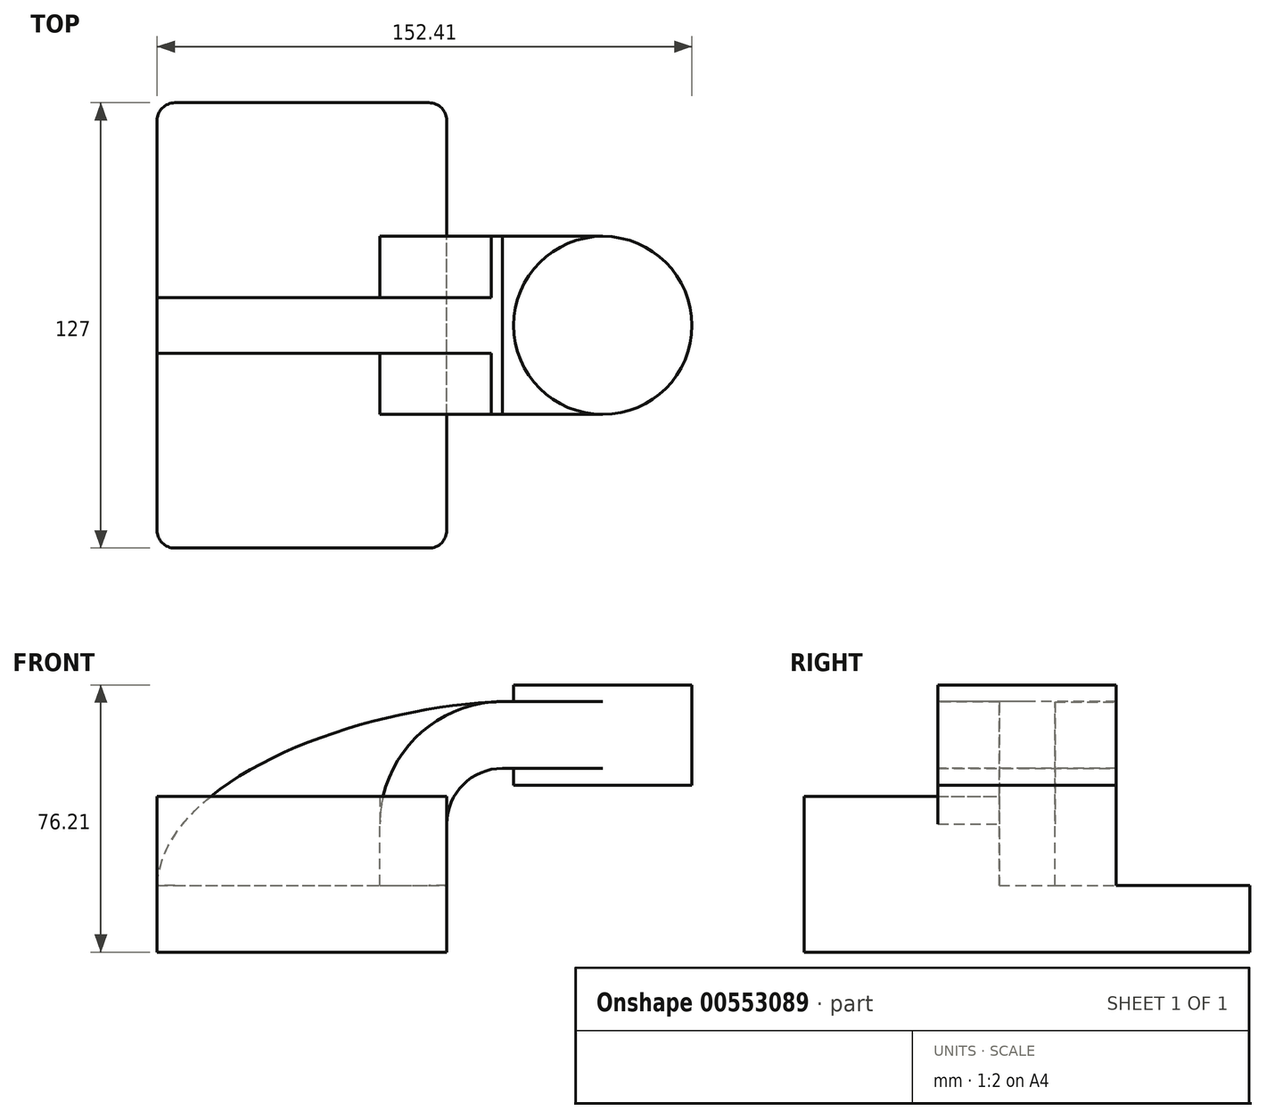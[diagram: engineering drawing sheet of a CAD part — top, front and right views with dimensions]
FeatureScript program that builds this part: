
annotation { "Feature Type Name" : "Feature", "Feature Type Description" : "" }
export const myFeature = defineFeature(function(context is Context, id is Id, definition is map)
    precondition{}
    {
        {
            var Q0;
            Q0=qCreatedBy(makeId("Front.planeOp"),FACE);
            var sketch = newSketch(context, id + "F0", { "sketchPlane" : qUnion([Q0])});
            skLineSegment(sketch, "E0.rect.bottom", {"start": v(-41.28, 9.52) * mm, "end": v(41.28, 9.52) * mm});
            skLineSegment(sketch, "E0.rect.top", {"start": v(-41.28, -9.52) * mm, "end": v(41.28, -9.52) * mm});
            skLineSegment(sketch, "E0.rect.left", {"start": v(-41.28, 9.52) * mm, "end": v(-41.28, -9.52) * mm});
            skLineSegment(sketch, "E0.rect.right", {"start": v(41.28, 9.52) * mm, "end": v(41.28, -9.52) * mm});
            skPoint(sketch, "E0.rect.middle", {"position": v(0, 0) * mm});
            skLineSegment(sketch, "E1", {"start": v(41.28, 9.52) * mm, "end": v(41.28, 27) * mm});
            skArc(sketch, "E2", {"start": v(41.28, 27) * mm, "mid": v(45.92, 38.23) * mm, "end": v(57.15, 42.88) * mm});
            skLineSegment(sketch, "E3", {"start": v(57.15, 42.88) * mm, "end": v(85.72, 42.88) * mm});
            skLineSegment(sketch, "E4.rect.bottom", {"start": v(60.32, 38.1) * mm, "end": v(111.12, 38.1) * mm});
            skLineSegment(sketch, "E4.rect.top", {"start": v(60.32, 66.68) * mm, "end": v(111.12, 66.68) * mm});
            skLineSegment(sketch, "E4.rect.left", {"start": v(60.32, 38.1) * mm, "end": v(60.32, 66.68) * mm});
            skLineSegment(sketch, "E4.rect.right", {"start": v(111.13, 38.1) * mm, "end": v(111.12, 66.68) * mm});
            skPoint(sketch, "E4.rect.middle", {"position": v(85.72, 52.39) * mm});
            skLineSegment(sketch, "E5.0", {"start": v(57.15, 61.93) * mm, "end": v(85.72, 61.93) * mm});
            skArc(sketch, "E5.1", {"start": v(22.23, 27) * mm, "mid": v(32.45, 51.7) * mm, "end": v(57.15, 61.93) * mm});
            skLineSegment(sketch, "E5.2", {"start": v(22.23, 9.52) * mm, "end": v(22.23, 27) * mm});
            skLineSegment(sketch, "E6", {"start": v(85.72, 38.1) * mm, "end": v(85.72, 66.68) * mm});
            skFitSpline(sketch, "E7", {"points": [v(-41.28, 9.53) * mm, v(57.15, 61.93) * mm], "startDerivative": vector(5.2, 92.34) * mm, "endDerivative": vector(120.92, 4.22) * mm});
            skSolve(sketch);
        }
        {
            var Q0;
            Q0=makeQuery(id+"F0.imprint","IMPRINT",FACE,{"disambiguationData":[TD([[makeQuery(id+"F0.imprint","IMPRINT",EDGE,{"derivedFrom":sQuery(id+"F0.wireOp",EDGE,"E0.rect.top")}),1.0]])]});
            extrude(context, id + "F1", {"entities" : qUnion([Q0]), "endBound" : BoundingType.SYMMETRIC, "depth" : 127 * mm});
        }
        {
            var Q0;
            {var subQ9=sQuery(id+"F0.wireOp",EDGE,"E1");Q0=makeQuery(id+"F0.imprint","IMPRINT",FACE,{"disambiguationData":[TD([[makeQuery(id+"F0.imprint","IMPRINT",EDGE,{"derivedFrom":subQ9}),1.0]])]});}
            var Q1;
            {var subQ0=sQuery(id+"F0.wireOp",EDGE,"E6");var subQ1=sQuery(id+"F0.wireOp",EDGE,"E3");var subQ2=makeQuery(id+"F0.imprint","INTERSECT",VERTEX,{"derivedFrom":[subQ1,subQ0]});Q1=makeQuery(id+"F0.imprint","IMPRINT",FACE,{"disambiguationData":[TD([[makeQuery(id+"F0.imprint","IMPRINT",EDGE,{"disambiguationData":[TD([[subQ2,1.0]])],"derivedFrom":subQ1}),1.0]])]});}
            extrude(context, id + "F2", {"entities" : qUnion([Q0, Q1]), "operationType" : NewBodyOperationType.ADD, "endBound" : BoundingType.SYMMETRIC, "depth" : 50.8 * mm});
        }
        {
            var Q0;
            {var subQ3=sQuery(id+"F0.wireOp",EDGE,"E5.2");Q0=makeQuery(id+"F0.imprint","IMPRINT",FACE,{"disambiguationData":[TD([[makeQuery(id+"F0.imprint","IMPRINT",EDGE,{"derivedFrom":subQ3}),1.0]])]});}
            extrude(context, id + "F3", {"entities" : qUnion([Q0]), "operationType" : NewBodyOperationType.ADD, "endBound" : BoundingType.SYMMETRIC, "depth" : 15.88 * mm});
        }
        {
            var Q0;
            {var subQ5=sQuery(id+"F0.wireOp",EDGE,"E4.rect.right");Q0=makeQuery(id+"F0.imprint","IMPRINT",FACE,{"disambiguationData":[TD([[makeQuery(id+"F0.imprint","IMPRINT",EDGE,{"derivedFrom":subQ5}),1.0]])]});}
            var Q1;
            Q1=sQuery(id+"F0.wireOp",EDGE,"E6");
            revolve(context, id + "F4", {"operationType" : NewBodyOperationType.ADD, "entities" : qUnion([Q0]), "axis" : qUnion([Q1]), "revolveType" : RevolveType.FULL});
        }
        {
            var Q0;
            Q0=makeQuery(id+"F1.opExtrude","CAP_EDGE",EDGE,{"disambiguationData":[OSD([sQuery(id+"F0.wireOp",EDGE,"E0.rect.right")])],"isStart":false});
            var Q1;
            Q1=makeQuery(id+"F1.opExtrude","CAP_EDGE",EDGE,{"disambiguationData":[OSD([sQuery(id+"F0.wireOp",EDGE,"E0.rect.left")])],"isStart":false});
            var Q2;
            Q2=makeQuery(id+"F1.opExtrude","CAP_EDGE",EDGE,{"disambiguationData":[OSD([sQuery(id+"F0.wireOp",EDGE,"E0.rect.right")])],"isStart":true});
            var Q3;
            Q3=makeQuery(id+"F1.opExtrude","CAP_EDGE",EDGE,{"disambiguationData":[OSD([sQuery(id+"F0.wireOp",EDGE,"E0.rect.left")])],"isStart":true});
            fillet(context, id + "F5", {"entities" : qUnion([Q0, Q1, Q2, Q3]), "radius" : 5.08 * mm, "tangentPropagation" : true, "allowEdgeOverflow" : false});
        }
        {
            var Q0;
            {var subQ4=sQuery(id+"F0.wireOp",EDGE,"E0.rect.bottom");var subQ5=sQuery(id+"F0.wireOp",EDGE,"E0.rect.right");var subQ6=sQuery(id+"F0.wireOp",EDGE,"E0.rect.left");Q0=makeQuery(id+"F3.boolean.opBoolean","SPLIT",FACE,{"disambiguationData":[TD([makeQuery(id+"F1.opExtrude","CAP_FACE",FACE,{"disambiguationData":[OSD([subQ4,sQuery(id+"F0.wireOp",EDGE,"E0.rect.top"),subQ6,subQ5])],"isStart":false})])],"derivedFrom":makeQuery(id+"F1.opExtrude","SWEPT_FACE",FACE,{"disambiguationData":[OSD([subQ4])]})});}
            extrude(context, id + "F6", {"entities" : qUnion([Q0]), "operationType" : NewBodyOperationType.ADD, "depth" : 25.4 * mm, "offsetDistance" : 25.4 * mm});
        }
    });
